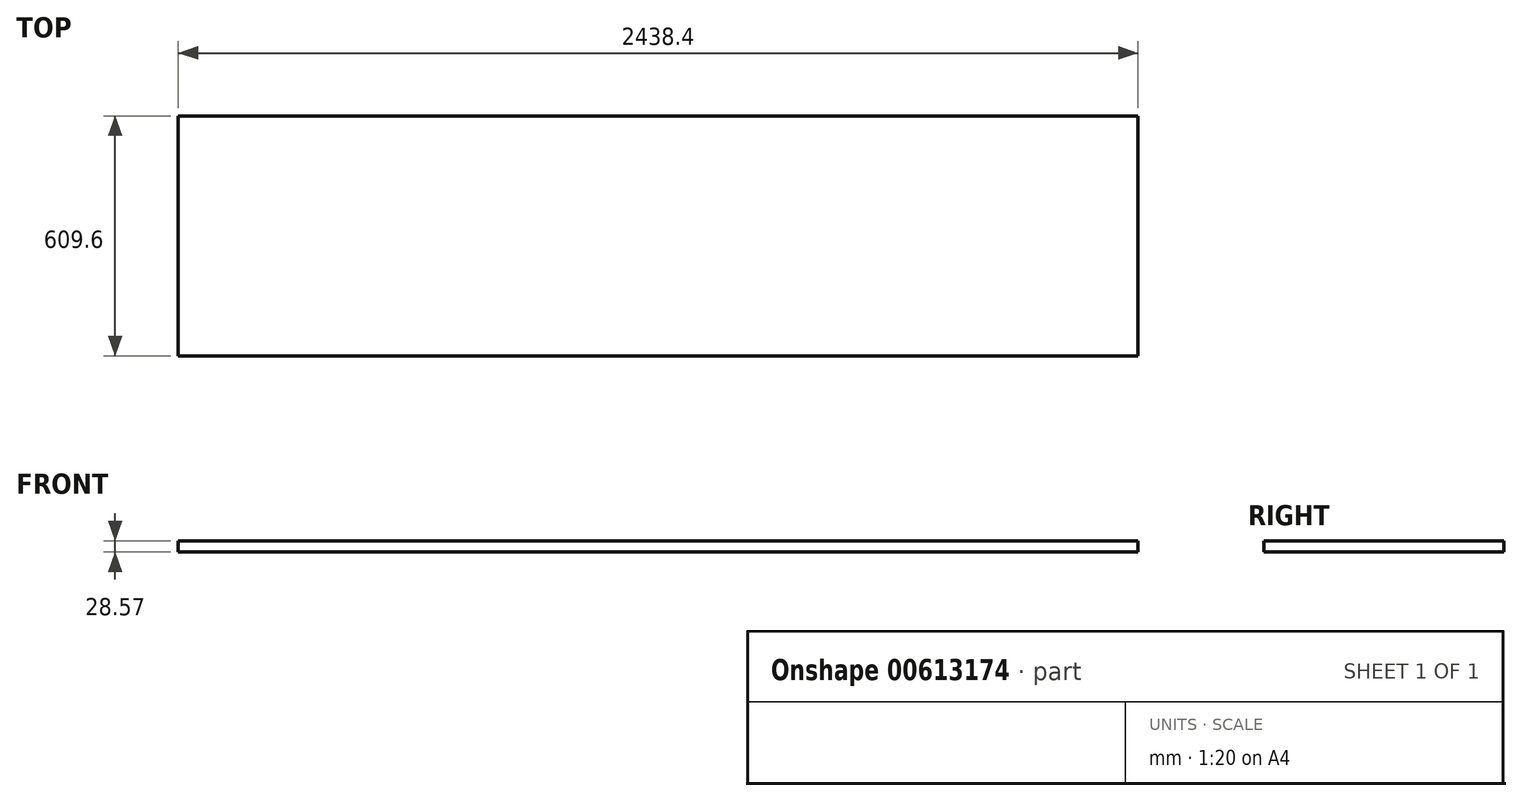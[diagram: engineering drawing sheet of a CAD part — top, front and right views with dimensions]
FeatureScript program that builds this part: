
annotation { "Feature Type Name" : "Feature", "Feature Type Description" : "" }
export const myFeature = defineFeature(function(context is Context, id is Id, definition is map)
    precondition{}
    {
        {
            var Q0;
            Q0=qCreatedBy(makeId("Top.planeOp"),FACE);
            var sketch = newSketch(context, id + "F0", { "sketchPlane" : qUnion([Q0])});
            skLineSegment(sketch, "E0.bottom", {"start": v(1219.2, 304.8) * mm, "end": v(-1219.2, 304.8) * mm});
            skLineSegment(sketch, "E0.top", {"start": v(1219.2, -304.8) * mm, "end": v(-1219.2, -304.8) * mm});
            skLineSegment(sketch, "E0.left", {"start": v(1219.2, 304.8) * mm, "end": v(1219.2, -304.8) * mm});
            skLineSegment(sketch, "E0.right", {"start": v(-1219.2, 304.8) * mm, "end": v(-1219.2, -304.8) * mm});
            skPoint(sketch, "E0.middle", {"position": v(0, 0) * mm});
            skSolve(sketch);
        }
        {
            var Q0;
            Q0=makeQuery(id+"F0.imprint","IMPRINT",FACE,{"disambiguationData":[TD([[makeQuery(id+"F0.imprint","IMPRINT",EDGE,{"derivedFrom":sQuery(id+"F0.wireOp",EDGE,"E0.bottom")}),1.0]])]});
            extrude(context, id + "F1", {"entities" : qUnion([Q0]), "depth" : 28.57 * mm, "offsetDistance" : 25.4 * mm});
        }
    });
